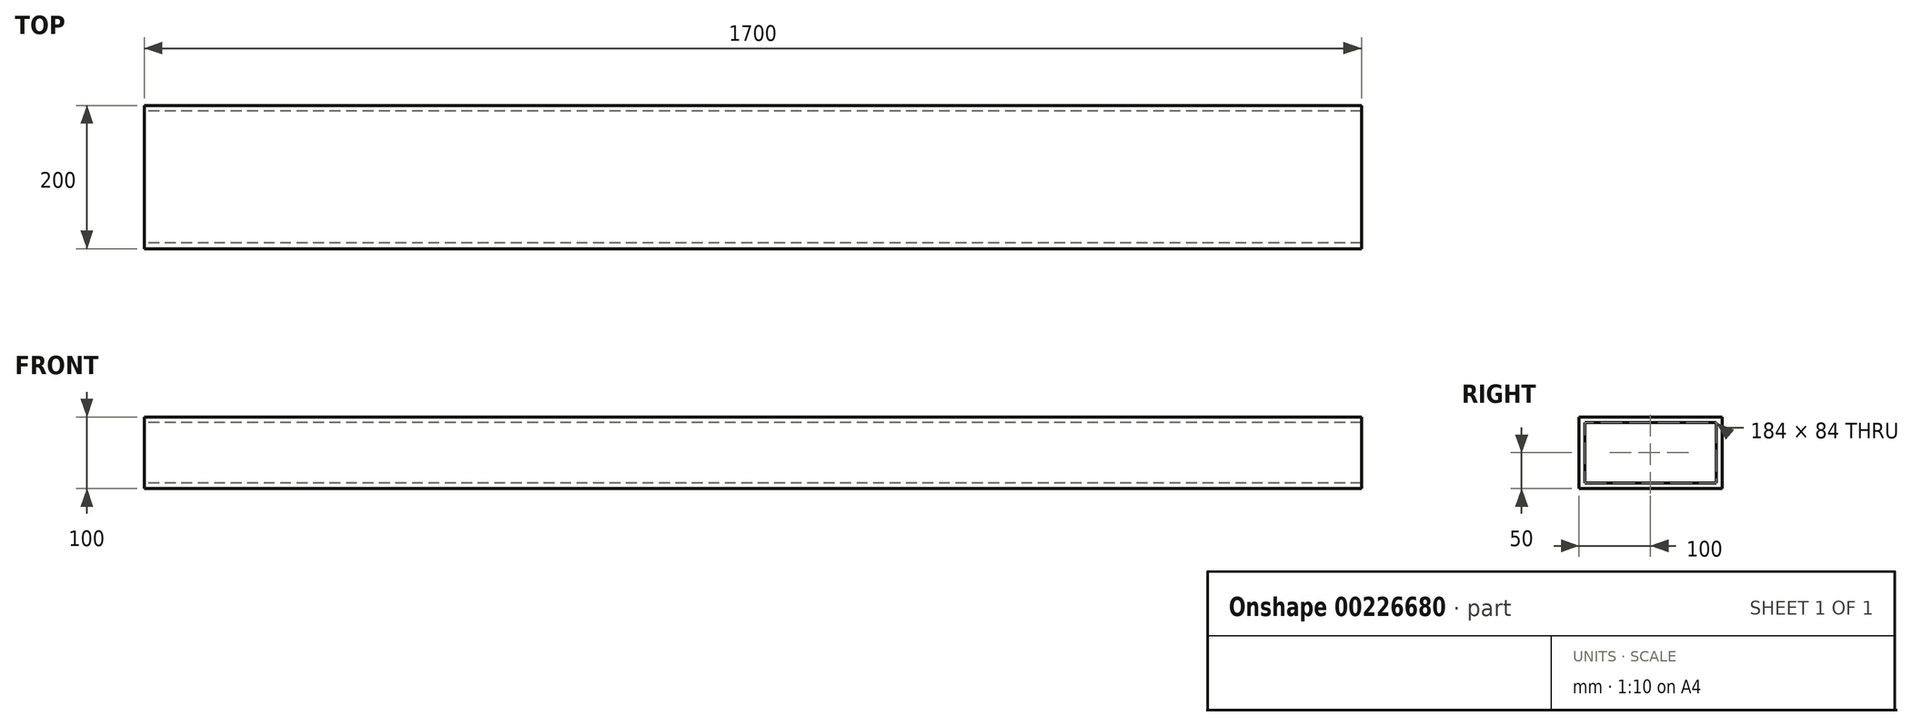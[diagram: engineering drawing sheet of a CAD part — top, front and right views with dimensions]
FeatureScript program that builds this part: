
annotation { "Feature Type Name" : "Feature", "Feature Type Description" : "" }
export const myFeature = defineFeature(function(context is Context, id is Id, definition is map)
    precondition{}
    {
        {
            var Q0;
            Q0=qCreatedBy(makeId("Right.planeOp"),FACE);
            var sketch = newSketch(context, id + "F0", { "sketchPlane" : qUnion([Q0])});
            skLineSegment(sketch, "E0.bottom", {"start": v(100, -50) * mm, "end": v(-100, -50) * mm});
            skLineSegment(sketch, "E0.top", {"start": v(100, 50) * mm, "end": v(-100, 50) * mm});
            skLineSegment(sketch, "E0.left", {"start": v(100, -50) * mm, "end": v(100, 50) * mm});
            skLineSegment(sketch, "E0.right", {"start": v(-100, -50) * mm, "end": v(-100, 50) * mm});
            skPoint(sketch, "E0.middle", {"position": v(0, 0) * mm});
            skLineSegment(sketch, "E1.bottom", {"start": v(92, -42) * mm, "end": v(-92, -42) * mm});
            skLineSegment(sketch, "E1.top", {"start": v(92, 42) * mm, "end": v(-92, 42) * mm});
            skLineSegment(sketch, "E1.left", {"start": v(92, -42) * mm, "end": v(92, 42) * mm});
            skLineSegment(sketch, "E1.right", {"start": v(-92, -42) * mm, "end": v(-92, 42) * mm});
            skSolve(sketch);
        }
        {
            var Q0;
            Q0=makeQuery(id+"F0.imprint","IMPRINT",FACE,{"disambiguationData":[TD([[makeQuery(id+"F0.imprint","IMPRINT",EDGE,{"derivedFrom":sQuery(id+"F0.wireOp",EDGE,"E0.bottom")}),-1.0]])]});
            extrude(context, id + "F1", {"entities" : qUnion([Q0]), "depth" : 1700 * mm});
        }
    });
